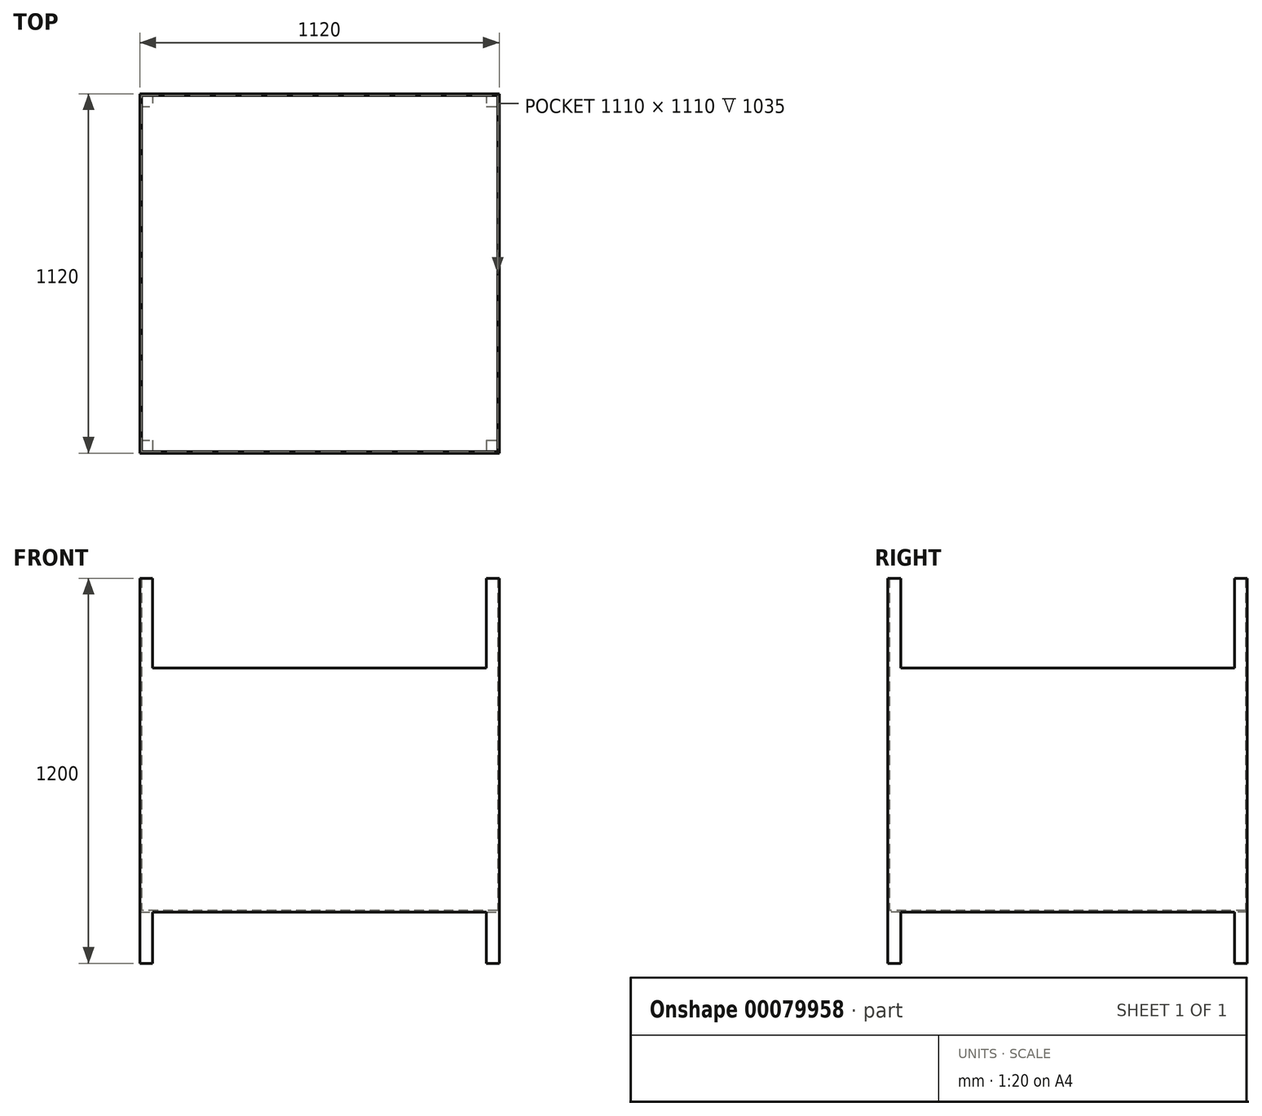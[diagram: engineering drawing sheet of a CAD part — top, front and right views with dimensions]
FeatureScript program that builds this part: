
annotation { "Feature Type Name" : "Feature", "Feature Type Description" : "" }
export const myFeature = defineFeature(function(context is Context, id is Id, definition is map)
    precondition{}
    {
        {
            var Q0;
            Q0=qCreatedBy(makeId("Top.planeOp"),FACE);
            var sketch = newSketch(context, id + "F0", { "sketchPlane" : qUnion([Q0])});
            skLineSegment(sketch, "E0.bottom", {"start": v(560, 560) * mm, "end": v(-560, 560) * mm});
            skLineSegment(sketch, "E0.top", {"start": v(560, -560) * mm, "end": v(-560, -560) * mm});
            skLineSegment(sketch, "E0.left", {"start": v(560, 560) * mm, "end": v(560, -560) * mm});
            skLineSegment(sketch, "E0.right", {"start": v(-560, 560) * mm, "end": v(-560, -560) * mm});
            skPoint(sketch, "E0.middle", {"position": v(0, 0) * mm});
            skSolve(sketch);
        }
        {
            var Q0;
            Q0 = qSketchRegion(id + "F0", true);
            extrude(context, id + "F1", {"entities" : qUnion([Q0]), "depth" : 1040 * mm});
        }
        {
            var Q0;
            Q0=makeQuery(id+"F1.opExtrude","CAP_FACE",FACE,{"disambiguationData":[OSD([sQuery(id+"F0.wireOp",EDGE,"E0.bottom"),sQuery(id+"F0.wireOp",EDGE,"E0.top"),sQuery(id+"F0.wireOp",EDGE,"E0.left"),sQuery(id+"F0.wireOp",EDGE,"E0.right")])],"isStart":false});
            shell(context, id + "F2", {"entities" : qUnion([Q0]), "thickness" : 5 * mm});
        }
        {
            var Q0;
            Q0 = qSketchRegion(id + "F0", true);
            extrude(context, id + "F3", {"entities" : qUnion([Q0]), "operationType" : NewBodyOperationType.ADD, "oppositeDirection" : true, "depth" : 160 * mm});
        }
        {
            var Q0;
            Q0=makeQuery(id+"F1.opExtrude","SWEPT_FACE",FACE,{"disambiguationData":[OSD([sQuery(id+"F0.wireOp",EDGE,"E0.top")])]});
            var sketch = newSketch(context, id + "F4", { "sketchPlane" : qUnion([Q0])});
            skLineSegment(sketch, "E1.bottom", {"start": v(520, 1040) * mm, "end": v(-520, 1040) * mm});
            skLineSegment(sketch, "E1.top", {"start": v(520, 760) * mm, "end": v(-520, 760) * mm});
            skLineSegment(sketch, "E1.left", {"start": v(520, 1040) * mm, "end": v(520, 760) * mm});
            skLineSegment(sketch, "E1.right", {"start": v(-520, 1040) * mm, "end": v(-520, 760) * mm});
            skLineSegment(sketch, "E2.bottom", {"start": v(-520, -160) * mm, "end": v(520, -160) * mm});
            skLineSegment(sketch, "E2.top", {"start": v(-520, 0) * mm, "end": v(520, 0) * mm});
            skLineSegment(sketch, "E2.left", {"start": v(-520, -160) * mm, "end": v(-520, 0) * mm});
            skLineSegment(sketch, "E2.right", {"start": v(520, -160) * mm, "end": v(520, 0) * mm});
            skSolve(sketch);
        }
        {
            var Q0;
            Q0 = qSketchRegion(id + "F4", true);
            extrude(context, id + "F5", {"entities" : qUnion([Q0]), "operationType" : NewBodyOperationType.REMOVE, "endBound" : BoundingType.THROUGH_ALL, "oppositeDirection" : true, "depth" : 25 * mm});
        }
        {
            var Q0;
            Q0=makeQuery(id+"F1.opExtrude","SWEPT_FACE",FACE,{"disambiguationData":[OSD([sQuery(id+"F0.wireOp",EDGE,"E0.left")])]});
            var sketch = newSketch(context, id + "F6", { "sketchPlane" : qUnion([Q0])});
            skLineSegment(sketch, "E3.bottom", {"start": v(-520, 1040) * mm, "end": v(520, 1040) * mm});
            skLineSegment(sketch, "E3.top", {"start": v(-520, 760) * mm, "end": v(520, 760) * mm});
            skLineSegment(sketch, "E3.left", {"start": v(-520, 1040) * mm, "end": v(-520, 760) * mm});
            skLineSegment(sketch, "E3.right", {"start": v(520, 1040) * mm, "end": v(520, 760) * mm});
            skLineSegment(sketch, "E4.bottom", {"start": v(-520, -160) * mm, "end": v(520, -160) * mm});
            skLineSegment(sketch, "E4.top", {"start": v(-520, 0) * mm, "end": v(520, 0) * mm});
            skLineSegment(sketch, "E4.left", {"start": v(-520, -160) * mm, "end": v(-520, 0) * mm});
            skLineSegment(sketch, "E4.right", {"start": v(520, -160) * mm, "end": v(520, 0) * mm});
            skSolve(sketch);
        }
        {
            var Q0;
            Q0 = qSketchRegion(id + "F6", true);
            extrude(context, id + "F7", {"entities" : qUnion([Q0]), "operationType" : NewBodyOperationType.REMOVE, "endBound" : BoundingType.THROUGH_ALL, "oppositeDirection" : true, "depth" : 25 * mm});
        }
    });
